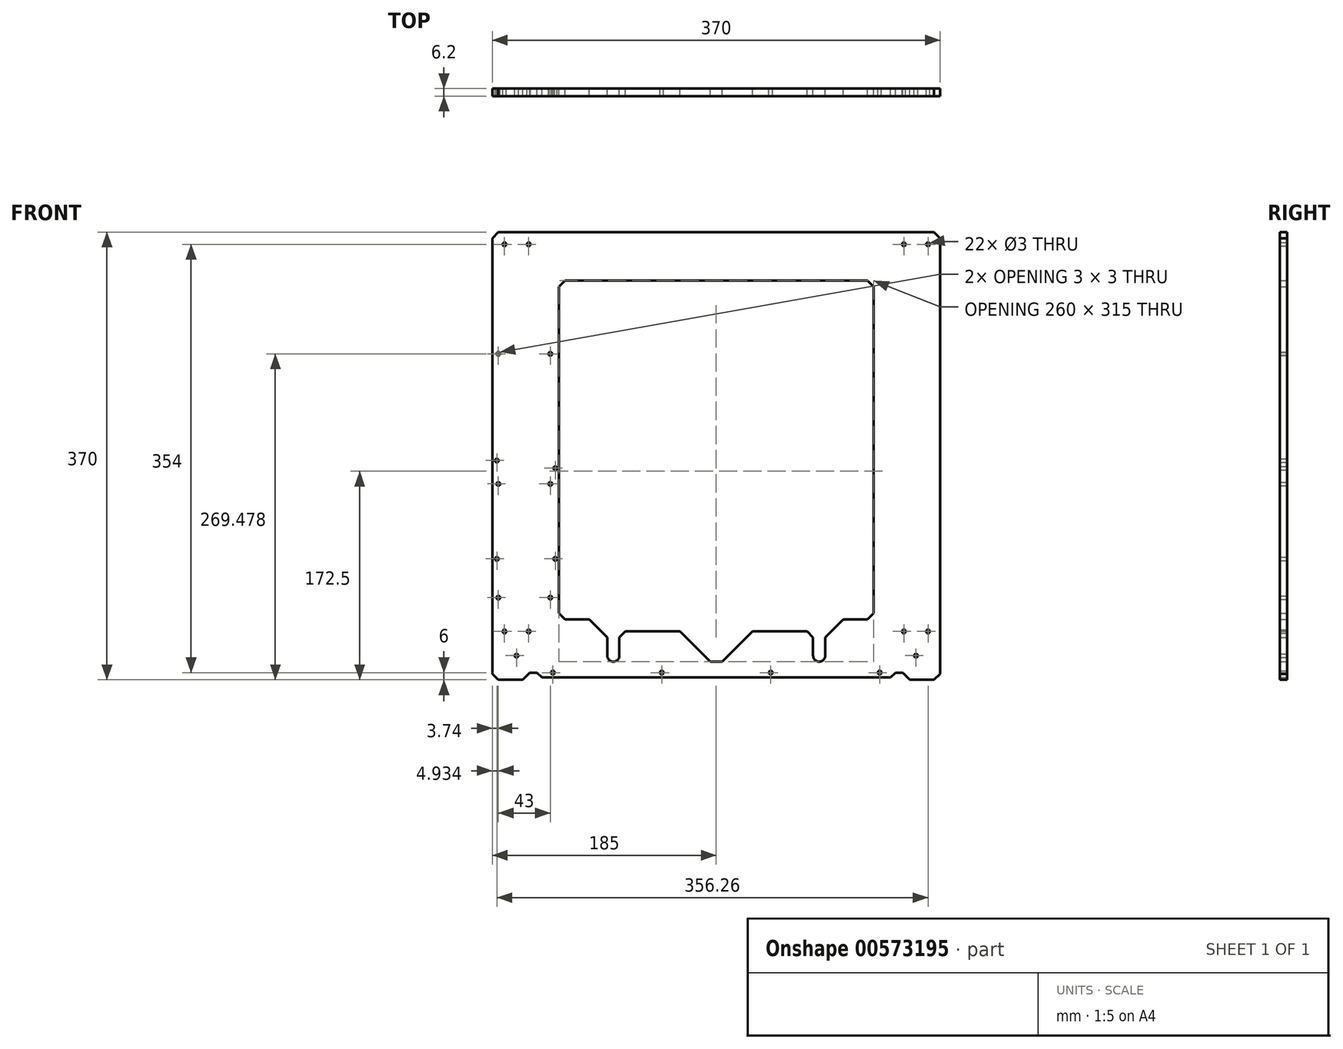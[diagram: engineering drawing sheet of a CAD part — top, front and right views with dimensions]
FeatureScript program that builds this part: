
annotation { "Feature Type Name" : "Feature", "Feature Type Description" : "" }
export const myFeature = defineFeature(function(context is Context, id is Id, definition is map)
    precondition{}
    {
        {
            var Q0;
            Q0=qCreatedBy(makeId("Front.planeOp"),FACE);
            var sketch = newSketch(context, id + "F0", { "sketchPlane" : qUnion([Q0])});
            skLineSegment(sketch, "E0", {"start": v(-180, -185) * mm, "end": v(-185, -180.2) * mm});
            skLineSegment(sketch, "E1", {"start": v(-185, -180.2) * mm, "end": v(-185, 180) * mm});
            skLineSegment(sketch, "E2", {"start": v(-185, 180) * mm, "end": v(-180, 185) * mm});
            skLineSegment(sketch, "E3", {"start": v(-180, 185) * mm, "end": v(180, 185) * mm});
            skLineSegment(sketch, "E4", {"start": v(180, 185) * mm, "end": v(185, 180) * mm});
            skLineSegment(sketch, "E5", {"start": v(185, 180) * mm, "end": v(185, -180) * mm});
            skLineSegment(sketch, "E6", {"start": v(185, -180) * mm, "end": v(180, -185) * mm});
            skLineSegment(sketch, "E7", {"start": v(180, -185) * mm, "end": v(160, -185) * mm});
            skLineSegment(sketch, "E8", {"start": v(160, -185) * mm, "end": v(158, -183) * mm});
            skLineSegment(sketch, "E9", {"start": v(144, -183) * mm, "end": v(-144, -183) * mm});
            skLineSegment(sketch, "E10", {"start": v(-158, -183) * mm, "end": v(-160, -185) * mm});
            skLineSegment(sketch, "E11", {"start": v(-160, -185) * mm, "end": v(-180, -185) * mm});
            skArc(sketch, "E12", {"start": v(-90, -165) * mm, "mid": v(-85, -170) * mm, "end": v(-80, -165) * mm});
            skLineSegment(sketch, "E13", {"start": v(-90, -165) * mm, "end": v(-90, -150) * mm});
            skLineSegment(sketch, "E14", {"start": v(-90, -150) * mm, "end": v(-105, -135) * mm});
            skLineSegment(sketch, "E15", {"start": v(-105, -135) * mm, "end": v(-125, -135) * mm});
            skLineSegment(sketch, "E16", {"start": v(-125, -135) * mm, "end": v(-130, -130) * mm});
            skLineSegment(sketch, "E17", {"start": v(-130, -130) * mm, "end": v(-130, 140) * mm});
            skLineSegment(sketch, "E18", {"start": v(-130, 140) * mm, "end": v(-125, 145) * mm});
            skLineSegment(sketch, "E19", {"start": v(-125, 145) * mm, "end": v(125, 145) * mm});
            skLineSegment(sketch, "E20", {"start": v(125, 145) * mm, "end": v(130, 140) * mm});
            skLineSegment(sketch, "E21", {"start": v(130, 140) * mm, "end": v(130, -130) * mm});
            skLineSegment(sketch, "E22", {"start": v(130, -130) * mm, "end": v(125, -135) * mm});
            skLineSegment(sketch, "E23", {"start": v(-80, -165) * mm, "end": v(-80, -150) * mm});
            skLineSegment(sketch, "E24", {"start": v(-80, -150) * mm, "end": v(-75, -145) * mm});
            skArc(sketch, "E25", {"start": v(80, -165) * mm, "mid": v(85, -170) * mm, "end": v(90, -165) * mm});
            skLineSegment(sketch, "E26", {"start": v(125, -135) * mm, "end": v(105, -135) * mm});
            skLineSegment(sketch, "E27", {"start": v(105, -135) * mm, "end": v(90, -150) * mm});
            skLineSegment(sketch, "E28", {"start": v(90, -150) * mm, "end": v(90, -165) * mm});
            skLineSegment(sketch, "E29", {"start": v(80, -165) * mm, "end": v(80, -150) * mm});
            skLineSegment(sketch, "E30", {"start": v(80, -150) * mm, "end": v(75, -145) * mm});
            skLineSegment(sketch, "E31", {"start": v(-5, -170) * mm, "end": v(5, -170) * mm});
            skLineSegment(sketch, "E32", {"start": v(5, -170) * mm, "end": v(30, -145) * mm});
            skLineSegment(sketch, "E33", {"start": v(-5, -170) * mm, "end": v(-30, -145) * mm});
            skLineSegment(sketch, "E34", {"start": v(-75, -145) * mm, "end": v(-30, -145) * mm});
            skLineSegment(sketch, "E35", {"start": v(30, -145) * mm, "end": v(75, -145) * mm});
            skCircle(sketch, "E36", {"center": v(-181.26, -3.72) * mm, "radius": 1.5 * mm});
            skCircle(sketch, "E37", {"center": v(-133, -10.07) * mm, "radius": 1.5 * mm});
            skCircle(sketch, "E38", {"center": v(-133, -85) * mm, "radius": 1.5 * mm});
            skCircle(sketch, "E39", {"center": v(-181.26, -85) * mm, "radius": 1.5 * mm});
            skLineSegment(sketch, "E40", {"start": v(158, -183) * mm, "end": v(154, -179) * mm});
            skLineSegment(sketch, "E41", {"start": v(154, -179) * mm, "end": v(148, -179) * mm});
            skLineSegment(sketch, "E42", {"start": v(148, -179) * mm, "end": v(144, -183) * mm});
            skLineSegment(sketch, "E43", {"start": v(-158, -183) * mm, "end": v(-154, -179) * mm});
            skLineSegment(sketch, "E44", {"start": v(-154, -179) * mm, "end": v(-148, -179) * mm});
            skLineSegment(sketch, "E45", {"start": v(-148, -179) * mm, "end": v(-144, -183) * mm});
            skCircle(sketch, "E46", {"center": v(-135, -179) * mm, "radius": 1.5 * mm});
            skCircle(sketch, "E47", {"center": v(135, -179) * mm, "radius": 1.5 * mm});
            skCircle(sketch, "E48", {"center": v(45, -179) * mm, "radius": 1.5 * mm});
            skCircle(sketch, "E49", {"center": v(-45, -179) * mm, "radius": 1.5 * mm});
            skCircle(sketch, "E50", {"center": v(-175, -145) * mm, "radius": 1.5 * mm});
            skCircle(sketch, "E51", {"center": v(-155, -145) * mm, "radius": 1.5 * mm});
            skCircle(sketch, "E52", {"center": v(-165, -165) * mm, "radius": 1.5 * mm});
            skCircle(sketch, "E53", {"center": v(165, -165) * mm, "radius": 1.5 * mm});
            skCircle(sketch, "E54", {"center": v(155, -145) * mm, "radius": 1.5 * mm});
            skCircle(sketch, "E55", {"center": v(175, -145) * mm, "radius": 1.5 * mm});
            skCircle(sketch, "E56", {"center": v(175, 175) * mm, "radius": 1.5 * mm});
            skCircle(sketch, "E57", {"center": v(155, 175) * mm, "radius": 1.5 * mm});
            skCircle(sketch, "E58", {"center": v(-175, 175) * mm, "radius": 1.5 * mm});
            skCircle(sketch, "E59", {"center": v(-155, 175) * mm, "radius": 1.5 * mm});
            skCircle(sketch, "E60", {"center": v(-137.05, -117.03) * mm, "radius": 1.5 * mm});
            skCircle(sketch, "E61", {"center": v(-180.05, -23.03) * mm, "radius": 1.5 * mm});
            skCircle(sketch, "E62", {"center": v(-137.05, -23.03) * mm, "radius": 1.5 * mm});
            skCircle(sketch, "E63", {"center": v(-180.05, 84.47) * mm, "radius": 1.5 * mm});
            skCircle(sketch, "E64", {"center": v(-137.05, 84.47) * mm, "radius": 1.5 * mm});
            skCircle(sketch, "E65", {"center": v(-180.08, -117) * mm, "radius": 1.5 * mm});
            skCircle(sketch, "E66", {"center": v(-180.08, 84.5) * mm, "radius": 1.5 * mm});
            skCircle(sketch, "E67", {"center": v(-137.08, 84.5) * mm, "radius": 1.5 * mm});
            skLineSegment(sketch, "E68", {"start": v(0, 185) * mm, "end": v(0, -183) * mm, "construction": true});
            skLineSegment(sketch, "E69", {"start": v(185, 0) * mm, "end": v(-185, 0) * mm, "construction": true});
            skSolve(sketch);
        }
        {
            var Q0;
            Q0=qSketchRegion(id+"F0",true);
            extrude(context, id + "F1", {"entities" : qUnion([Q0]), "depth" : 6.2 * mm, "offsetDistance" : 25 * mm});
        }
    });
